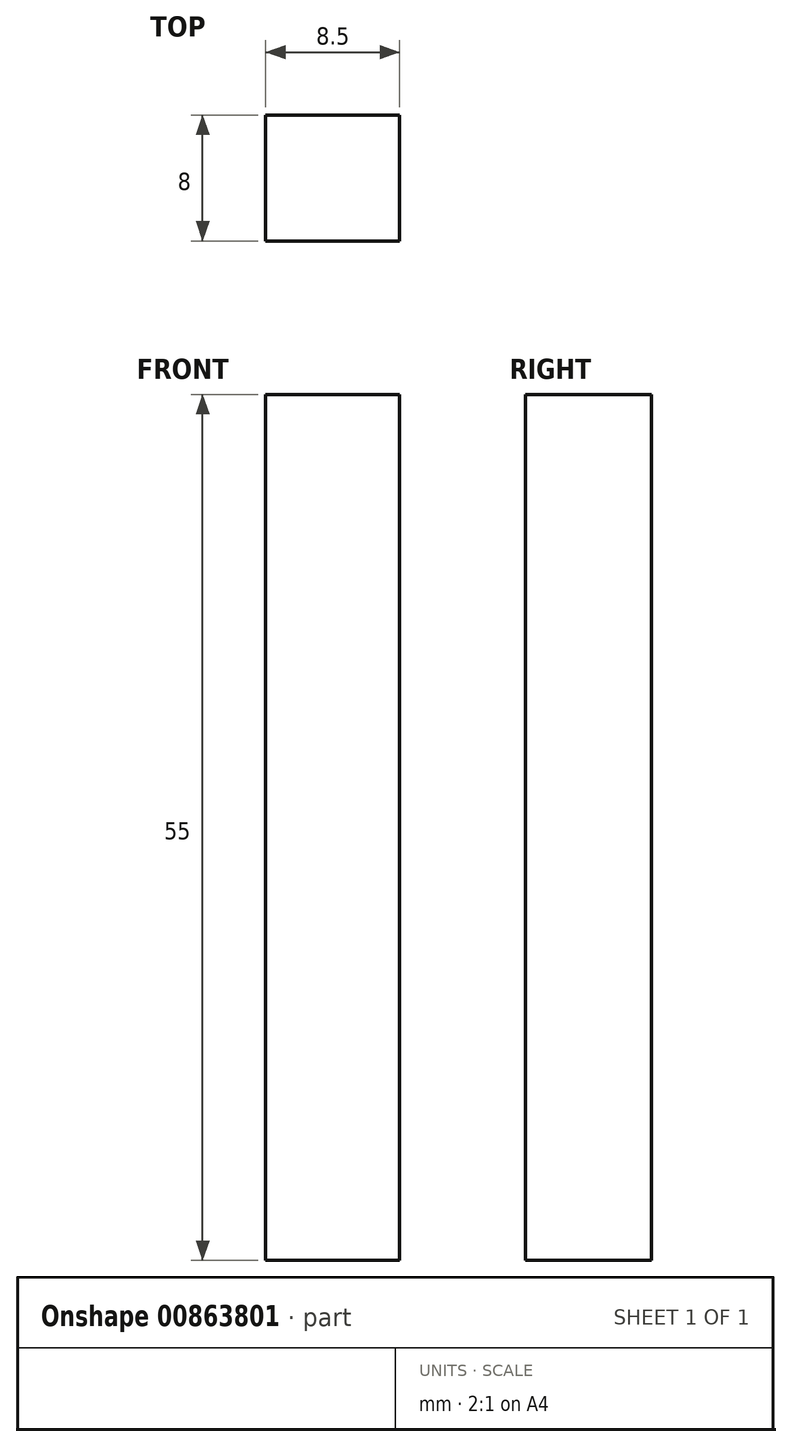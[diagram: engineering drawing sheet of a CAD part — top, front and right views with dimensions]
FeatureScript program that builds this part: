
annotation { "Feature Type Name" : "Feature", "Feature Type Description" : "" }
export const myFeature = defineFeature(function(context is Context, id is Id, definition is map)
    precondition{}
    {
        {
            var Q0;
            Q0=qCreatedBy(makeId("Top.planeOp"),FACE);
            var sketch = newSketch(context, id + "F0", { "sketchPlane" : qUnion([Q0])});
            skLineSegment(sketch, "E0.bottom", {"start": v(0, 0) * mm, "end": v(8.5, 0) * mm});
            skLineSegment(sketch, "E0.top", {"start": v(0, 8) * mm, "end": v(8.5, 8) * mm});
            skLineSegment(sketch, "E0.left", {"start": v(0, 0) * mm, "end": v(0, 8) * mm});
            skLineSegment(sketch, "E0.right", {"start": v(8.5, 0) * mm, "end": v(8.5, 8) * mm});
            skSolve(sketch);
        }
        {
            var Q0;
            Q0 = qSketchRegion(id + "F0", true);
            extrude(context, id + "F1", {"entities" : qUnion([Q0]), "depth" : 55 * mm, "offsetDistance" : 25 * mm});
        }
    });
